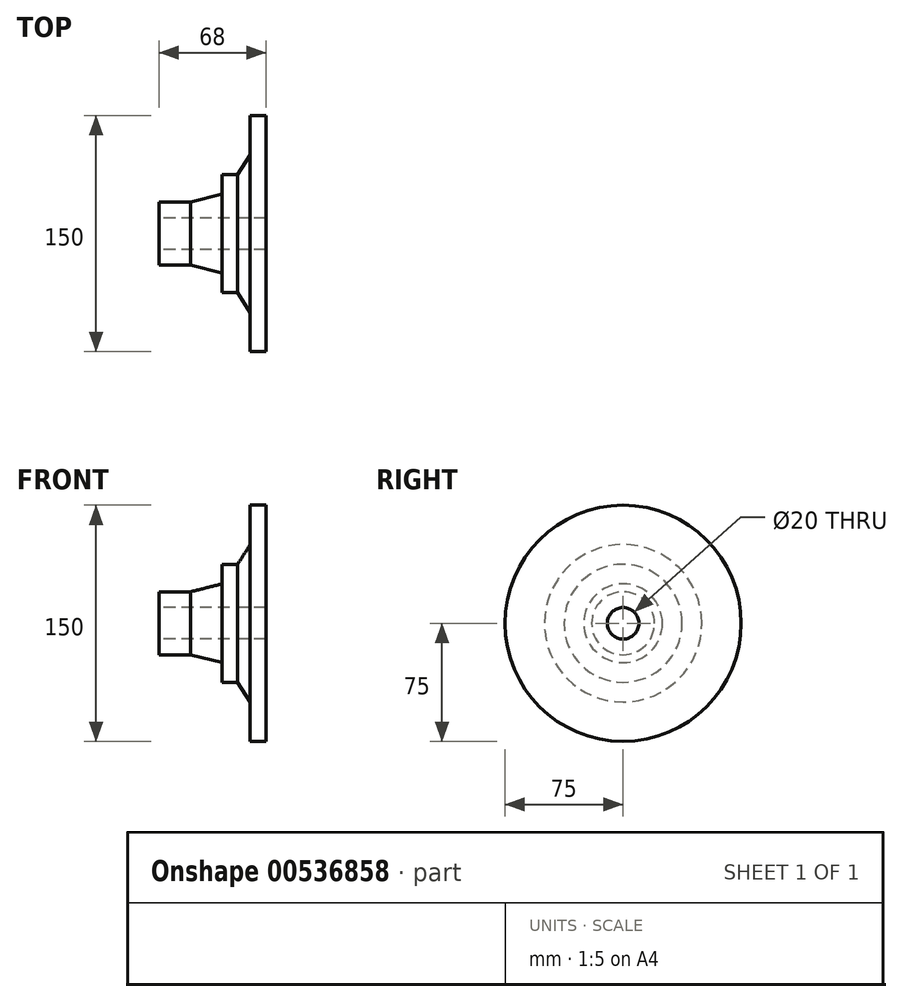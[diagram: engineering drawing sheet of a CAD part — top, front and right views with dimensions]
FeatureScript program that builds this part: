
annotation { "Feature Type Name" : "Feature", "Feature Type Description" : "" }
export const myFeature = defineFeature(function(context is Context, id is Id, definition is map)
    precondition{}
    {
        {
            var Q0;
            Q0=qCreatedBy(makeId("Front.planeOp"),FACE);
            var sketch = newSketch(context, id + "F0", { "sketchPlane" : qUnion([Q0])});
            skLineSegment(sketch, "E0", {"start": v(-34.33, 0) * mm, "end": v(33.67, 0) * mm});
            skSolve(sketch);
        }
        {
            var Q0;
            Q0=qCreatedBy(makeId("Front.planeOp"),FACE);
            var sketch = newSketch(context, id + "F1", { "sketchPlane" : qUnion([Q0])});
            skLineSegment(sketch, "E1.0", {"start": v(-34.33, -10) * mm, "end": v(33.67, -10) * mm});
            skLineSegment(sketch, "E2", {"start": v(-34.33, -10) * mm, "end": v(-34.33, -20) * mm});
            skLineSegment(sketch, "E3", {"start": v(-34.33, -20) * mm, "end": v(-14.33, -20) * mm});
            skLineSegment(sketch, "E4", {"start": v(33.67, -10) * mm, "end": v(33.67, -75) * mm});
            skLineSegment(sketch, "E5", {"start": v(33.67, -75) * mm, "end": v(23.67, -75) * mm});
            skLineSegment(sketch, "E6.0", {"start": v(5.67, -37.5) * mm, "end": v(15.67, -37.5) * mm});
            skLineSegment(sketch, "E7.0", {"start": v(23.67, -50) * mm, "end": v(23.67, -75) * mm});
            skLineSegment(sketch, "E8.0", {"start": v(5.67, -25) * mm, "end": v(5.67, -37.5) * mm});
            skLineSegment(sketch, "E9", {"start": v(-14.33, -20) * mm, "end": v(5.67, -25) * mm});
            skLineSegment(sketch, "E10", {"start": v(15.67, -37.5) * mm, "end": v(23.67, -50) * mm});
            skLineSegment(sketch, "E11", {"start": v(-14.33, -20) * mm, "end": v(-34.33, -20) * mm});
            skSolve(sketch);
        }
        {
            var Q0;
            Q0=makeQuery(id+"F1.imprint","IMPRINT",FACE,{"disambiguationData":[TD([[makeQuery(id+"F1.imprint","IMPRINT",EDGE,{"derivedFrom":sQuery(id+"F1.wireOp",EDGE,"E1.0")}),-1.0]])]});
            var Q1;
            Q1=sQuery(id+"F0.wireOp",EDGE,"E0");
            revolve(context, id + "F2", {"entities" : qUnion([Q0]), "axis" : qUnion([Q1]), "revolveType" : RevolveType.FULL});
        }
    });
